# Revit family: Deca_Lavatório_Vogue Plus_L.510
name_source: partatom
category: Plumbing Fixtures
units: mm (PartAtom-declared; Revit-internal decimal feet)

## family parameters
Cut with Voids When Loaded = No
Host = Face
Part Type = Normal
Room Calculation Point = No
Round Connector Dimension = Use Radius
Shared = No

## types (5) — shared parameters
Acompanha o Produto = -
Aprovado por = quattroD
Atendimento ao Cliente = 0800-0117073
Categoria = LAVATORIOS
Com Coluna = Yes
Composição Anel Vedação = -
Composição Assento = -
Composição Básica = Argila, feldspato, caulim, vidrados e corantes inorgânicos.
Composição Componente = Não Possui
Consumo = -
Cor Interna = -
Cor Secundária = -
Cores Componente = Não Possui
Criado por = quattroD
Código Pai = L.510
Default Elevation = 0.8 m
Description = Lavatório
Diâmetro Ponto de Esgoto = 0.03 m
Informações Complementares = -
Itens de Instalação = 1601.C; 1601.C.CLI; 1602.C; 1602.C.PLA; 1680.C.100.112; 1682.C.100.112; 1684.C.100.112; C.10.17; C.510.17; SP.13.01; SP.7.01
Linha = Vogue Plus
Manufacturer = Deca
Norma = NBR-16728-1;NBR-16728-2
Pressão máx. funcionamento = -
Pressão mín. Aquec. Acúmulo = -
Pressão mín. Aquec. Passagem = -
Pressão mín. funcionamento = -
Raio Ponto de Esgoto = 0.01 m
Saída de Esgoto = Válvula Longa
Segmento = Banheiro Competitivo
Tipo de dispositivo economizador = -
Tipo de mecanismo utilizado = -
Tipo de rosca de entrada = -
Tipo de rosca de saída = -
URL = www.deca.com.br
Vazão na Pressão máx. (L/min) = -
Vazão na Pressão mín. (L/min) = -

## per-type parameters (varying)
| type | Combinação | Cor Principal | Material | Model | Peso Líquido (Kg) |
| L.510.17_Branco_C.10.17 | Deca_Coluna para lavatório_Aspen_C.10 : C.10.17_Branco | Branco | Deca_Branco | L.510.17 | 10.413 |
| L.510.37_Creme_C.10.37 | Deca_Coluna para lavatório_Aspen_C.10 : C.10.37_Creme | Creme | Deca_Creme | L.510.37 | 10.413 |
| L.510.60_Verde_C.10.60 | Deca_Coluna para lavatório_Aspen_C.10 : C.10.60_Verde | Verde | Deca_Verde | L.510.60 | 9.033 |
| L.510.87_Cinza Real_C.10.87 | Deca_Coluna para lavatório_Aspen_C.10 : C.10.87_Cinza Real | Cinza Real | Deca_Cinza | L.510.87 | 10.413 |
| L.510.95_Ébano_C.10.95 | Deca_Coluna para lavatório_Aspen_C.10 : C.10.95_Ébano | Ébano | Deca_Ébano | L.510.95 | 10.413 |

## geometry (parser evidence)
native form markers: Sweep x6
no freeform markers — native parametric forms only
